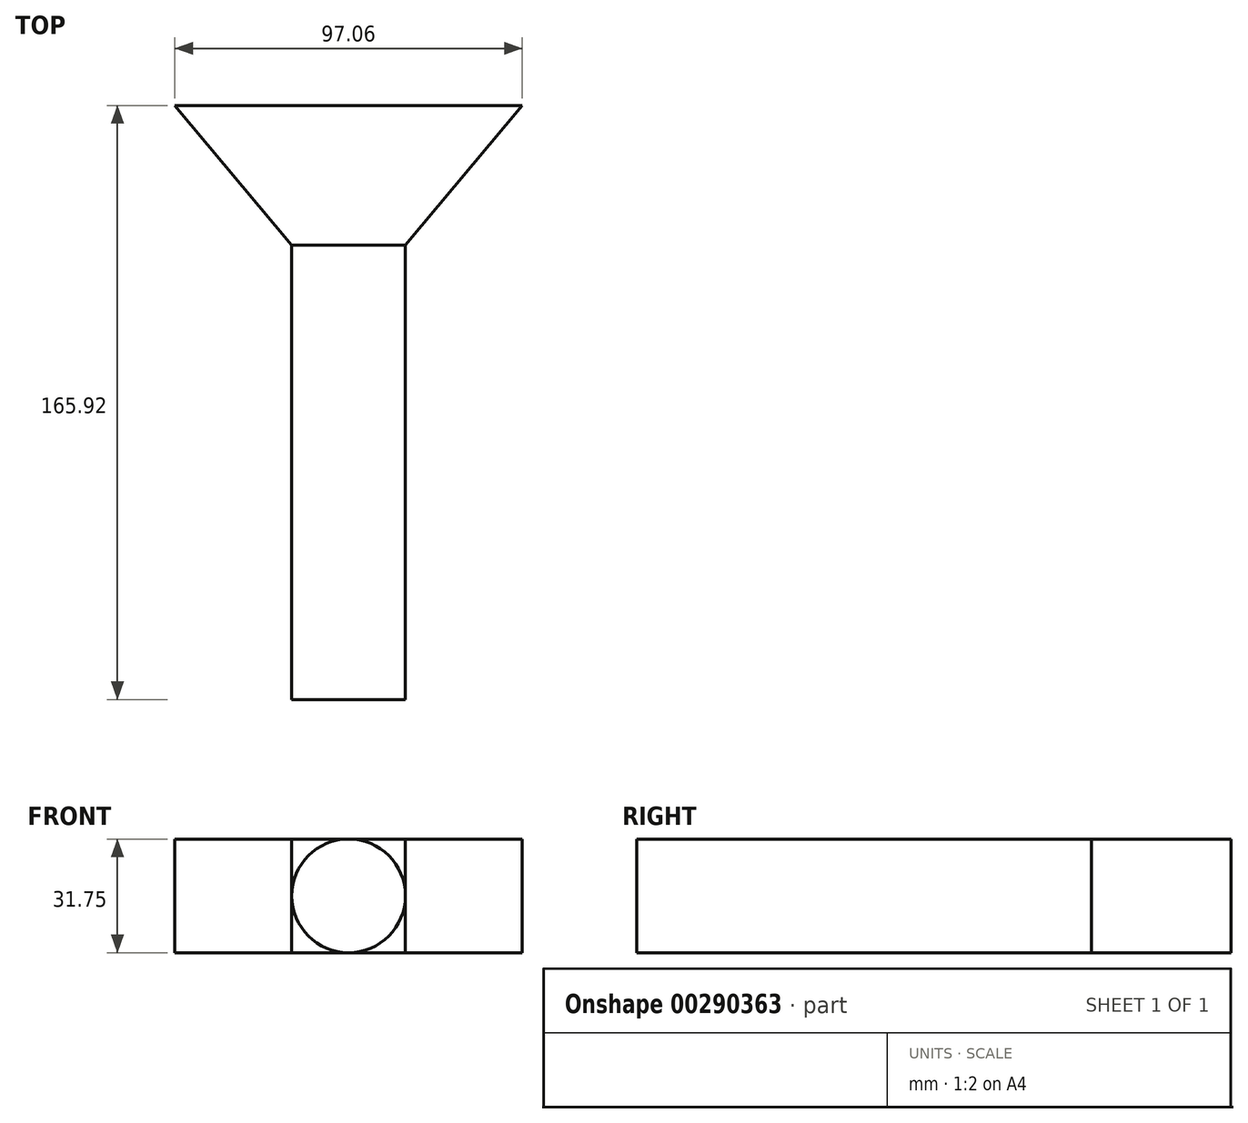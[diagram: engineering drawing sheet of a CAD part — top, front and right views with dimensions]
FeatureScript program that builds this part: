
annotation { "Feature Type Name" : "Feature", "Feature Type Description" : "" }
export const myFeature = defineFeature(function(context is Context, id is Id, definition is map)
    precondition{}
    {
        {
            var Q0;
            Q0=qCreatedBy(makeId("Top.planeOp"),FACE);
            var sketch = newSketch(context, id + "F0", { "sketchPlane" : qUnion([Q0])});
            skLineSegment(sketch, "E0", {"start": v(-15.87, 0) * mm, "end": v(15.87, 0) * mm});
            skLineSegment(sketch, "E1", {"start": v(-15.87, 0) * mm, "end": v(-48.53, 38.92) * mm});
            skLineSegment(sketch, "E2", {"start": v(-48.53, 38.92) * mm, "end": v(48.53, 38.92) * mm});
            skLineSegment(sketch, "E3", {"start": v(15.87, 0) * mm, "end": v(48.53, 38.92) * mm});
            skSolve(sketch);
        }
        {
            var Q0;
            Q0 = qSketchRegion(id + "F0", true);
            var Q1;
            Q1 = qSketchRegion(id + "F2", true);
            extrude(context, id + "F1", {"entities" : qUnion([Q0, Q1]), "depth" : 31.75 * mm});
        }
        {
            var Q0;
            Q0=makeQuery(id+"F1.opExtrude","SWEPT_FACE",FACE,{"disambiguationData":[OSD([sQuery(id+"F0.wireOp",EDGE,"E0")])]});
            var sketch = newSketch(context, id + "F2", { "sketchPlane" : qUnion([Q0])});
            skCircle(sketch, "E4", {"center": v(0, 15.88) * mm, "radius": 15.88 * mm});
            skPoint(sketch, "E4.centerSnap0", {"position": v(0, 0) * mm});
            skPoint(sketch, "E4.centerSnap1", {"position": v(-15.87, 15.88) * mm});
            skSolve(sketch);
        }
        {
            var Q0;
            {var subQ0=sQuery(id+"F2.wireOp",EDGE,"E4");var subQ1=sQuery(id+"F0.wireOp",EDGE,"E0");var subQ2=makeQuery(id+"F2.imprint","INTERSECT",VERTEX,{"derivedFrom":[makeQuery(id+"F1.opExtrude","CAP_EDGE",EDGE,{"disambiguationData":[OSD([subQ1])],"isStart":false}),subQ0]});Q0=makeQuery(id+"F2.imprint","IMPRINT",FACE,{"disambiguationData":[TD([[makeQuery(id+"F2.imprint","IMPRINT",EDGE,{"disambiguationData":[TD([[subQ2,1.0]])],"derivedFrom":subQ0}),1.0]])]});}
            extrude(context, id + "F3", {"entities" : qUnion([Q0]), "operationType" : NewBodyOperationType.ADD, "depth" : 127 * mm});
        }
    });
